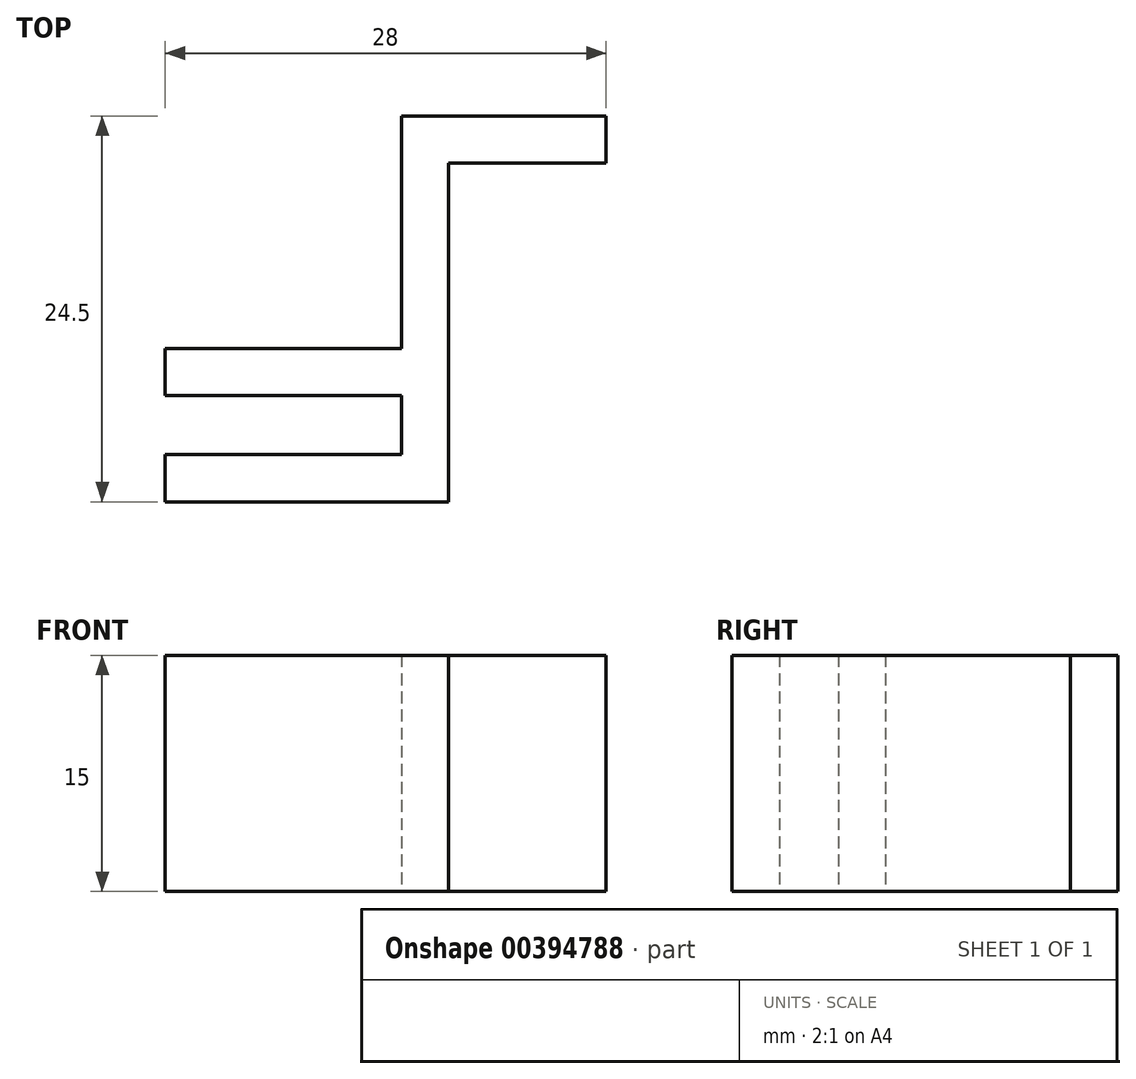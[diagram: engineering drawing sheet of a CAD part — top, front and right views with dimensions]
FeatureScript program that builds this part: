
annotation { "Feature Type Name" : "Feature", "Feature Type Description" : "" }
export const myFeature = defineFeature(function(context is Context, id is Id, definition is map)
    precondition{}
    {
        {
            var Q0;
            Q0=qCreatedBy(makeId("Top.planeOp"),FACE);
            var sketch = newSketch(context, id + "F0", { "sketchPlane" : qUnion([Q0])});
            skLineSegment(sketch, "E0", {"start": v(-18, 0) * mm, "end": v(0, 0) * mm});
            skLineSegment(sketch, "E1", {"start": v(0, 0) * mm, "end": v(0, 21.5) * mm});
            skLineSegment(sketch, "E2", {"start": v(0, 21.5) * mm, "end": v(10, 21.5) * mm});
            skLineSegment(sketch, "E3", {"start": v(10, 21.5) * mm, "end": v(10, 24.5) * mm});
            skLineSegment(sketch, "E4", {"start": v(10, 24.5) * mm, "end": v(-3, 24.5) * mm});
            skLineSegment(sketch, "E5", {"start": v(-3, 24.5) * mm, "end": v(-3, 9.75) * mm});
            skLineSegment(sketch, "E6", {"start": v(-3, 9.75) * mm, "end": v(-18, 9.75) * mm});
            skLineSegment(sketch, "E7", {"start": v(-18, 9.75) * mm, "end": v(-18, 6.75) * mm});
            skLineSegment(sketch, "E8", {"start": v(-18, 6.75) * mm, "end": v(-3, 6.75) * mm});
            skLineSegment(sketch, "E9", {"start": v(-3, 6.75) * mm, "end": v(-3, 3) * mm});
            skLineSegment(sketch, "E10", {"start": v(-3, 3) * mm, "end": v(-18, 3) * mm});
            skLineSegment(sketch, "E11", {"start": v(-18, 3) * mm, "end": v(-18, 0) * mm});
            skSolve(sketch);
        }
        {
            var Q0;
            Q0=makeQuery(id+"F0.imprint","IMPRINT",FACE,{"disambiguationData":[TD([[makeQuery(id+"F0.imprint","IMPRINT",EDGE,{"derivedFrom":sQuery(id+"F0.wireOp",EDGE,"E0")}),1.0]])]});
            extrude(context, id + "F1", {"entities" : qUnion([Q0]), "depth" : 15 * mm});
        }
    });
